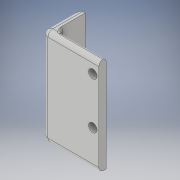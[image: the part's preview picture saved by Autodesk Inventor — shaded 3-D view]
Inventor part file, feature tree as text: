
AUTODESK INVENTOR PART (.ipt)
format: ipt  version: 2019.4 (Build 234330000, 330)  size: 214,016 bytes
history: native  units: mm
features: fillet x5, extrude x4, sketch x4, plane x1
ambient origin geometry x8: Origin, YZ Plane, XZ Plane, XY Plane, X Axis, Y Axis, Z Axis, Center Point
bodies: Solid1 (feature_tree)
feature tree (14):
  extrude  "Extrusion1"  Depth=3.0mm
  extrude  "Extrusion2"  Depth=3.0mm
  fillet  "Fillet1"  Radius=40.0mm
  fillet  "Fillet2"  Radius=2.5mm
  fillet  "Fillet3"  Radius=15.0mm
  extrude  "Extrusion3"  Depth=3.5mm
  plane  "Work Plane1"
  extrude  "Extrusion4"  TaperAngle=90.0deg  [1 undecoded]
  fillet  "Fillet4"  Radius=3.5mm
  fillet  "Fillet5"  Radius=3.0mm
  sketch  "Sketch1"  dims[d0=20.0mm d1=3.0mm]
  sketch  "Sketch2"  dims[d2=15.0mm d3=3.0mm d4=40.0mm d5=0.0mm d6=2.5mm d7=15.0mm]
  sketch  "Sketch3"  dims[d8=90.0deg d9=3.5mm]
  sketch  "Sketch4"  dims[d10=19.175mm d11=90.0deg d12=3.5mm d13=3.0mm d14=0.0mm d15=2.0mm d16=2.0mm d17=2.0mm d18=10.0mm d19=90.0deg d20=6.5mm d21=10.0mm d22=90.0deg d23=3.5mm d24=3.5mm d25=3.0mm d26=0.0mm d27=-22.0mm d30=12.0mm d31=3.0mm d32=0.0mm d33=2.5mm d34=2.5mm]
note: 1 required parameter value undecoded (feature->parameter linkage not recoverable at this tier; creation-order binding heuristic only, values carry confidence <= 0.55)
